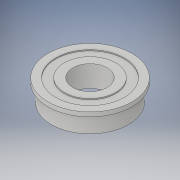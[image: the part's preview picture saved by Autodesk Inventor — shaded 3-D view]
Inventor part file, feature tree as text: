
AUTODESK INVENTOR PART (.ipt)
format: ipt  version: 2019.3 (Build 233278000, 278)  size: 137,728 bytes
history: native  units: in
note: dims shown in document units (in); Inventor stores cm internally (conversion verified against a paired STEP export)
features: revolve x1
ambient origin geometry x8: Origin, YZ Plane, XZ Plane, XY Plane, X Axis, Y Axis, Z Axis, Center Point
bodies: Solid1 (feature_tree)
feature tree (1):
  revolve  "Revolve1"  [1 undecoded]
note: 1 required parameter value undecoded (feature->parameter linkage not recoverable at this tier; creation-order binding heuristic only, values carry confidence <= 0.55)
